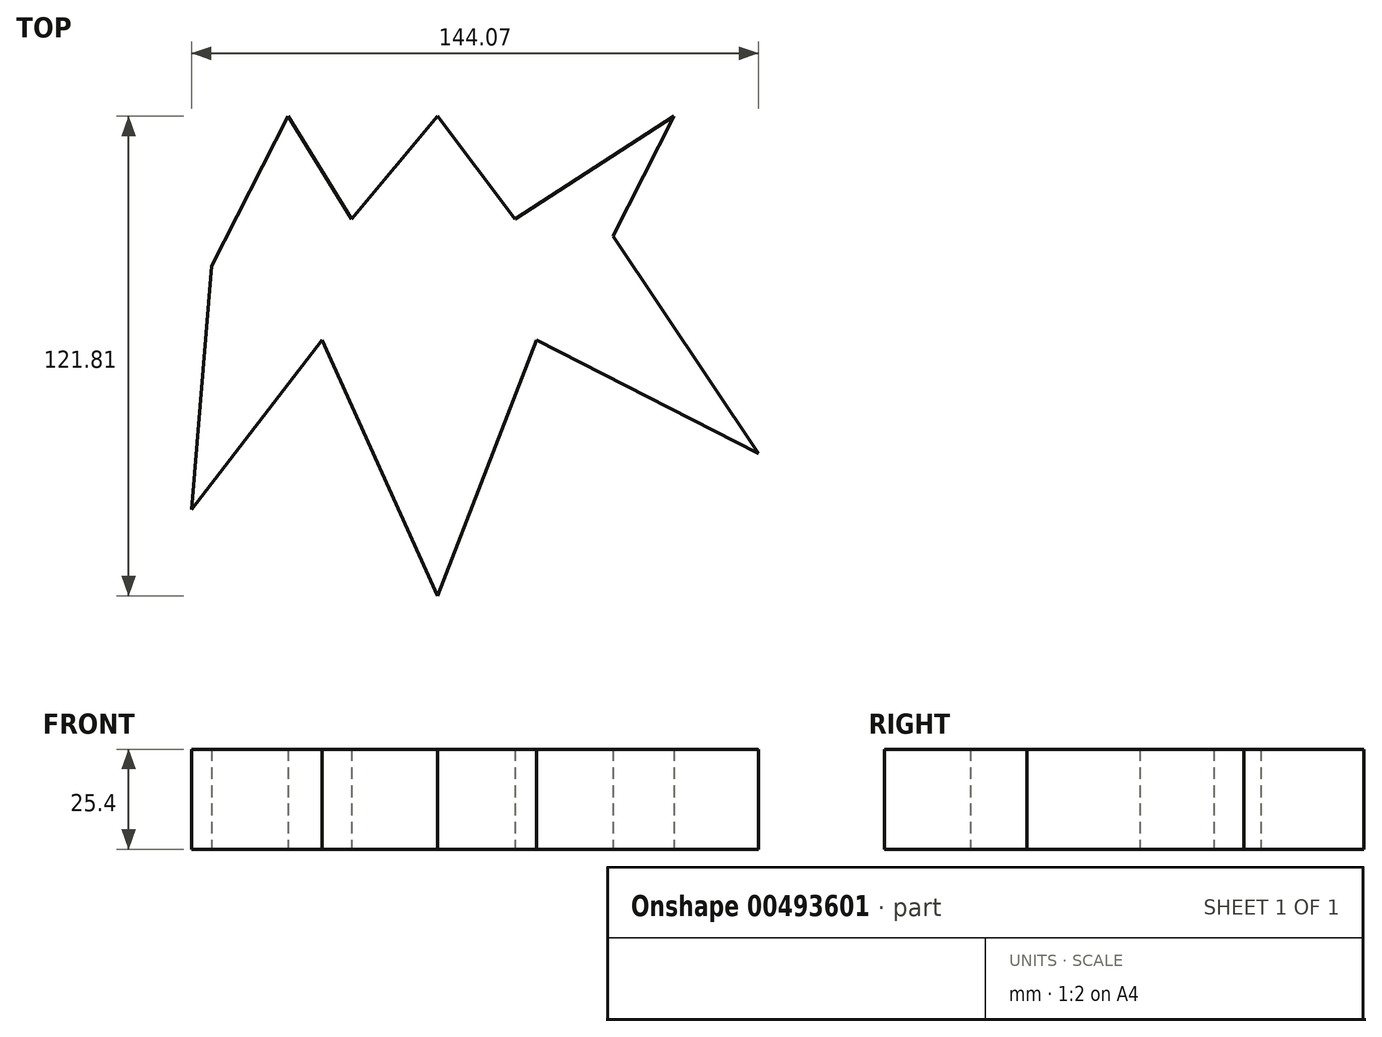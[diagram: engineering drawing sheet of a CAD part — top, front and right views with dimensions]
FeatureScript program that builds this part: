
annotation { "Feature Type Name" : "Feature", "Feature Type Description" : "" }
export const myFeature = defineFeature(function(context is Context, id is Id, definition is map)
    precondition{}
    {
        {
            var Q0;
            Q0=qCreatedBy(makeId("Top.planeOp"),FACE);
            var sketch = newSketch(context, id + "F0", { "sketchPlane" : qUnion([Q0])});
            skLineSegment(sketch, "E0", {"start": v(-67.12, 9.7) * mm, "end": v(-47.69, 47.8) * mm});
            skLineSegment(sketch, "E1", {"start": v(-47.69, 47.8) * mm, "end": v(-31.56, 21.65) * mm});
            skLineSegment(sketch, "E2", {"start": v(-31.56, 21.65) * mm, "end": v(-9.73, 47.8) * mm});
            skLineSegment(sketch, "E3", {"start": v(-9.73, 47.8) * mm, "end": v(9.99, 21.65) * mm});
            skLineSegment(sketch, "E4", {"start": v(9.99, 21.65) * mm, "end": v(50.35, 47.8) * mm});
            skLineSegment(sketch, "E5", {"start": v(50.35, 47.8) * mm, "end": v(34.82, 17.36) * mm});
            skLineSegment(sketch, "E6", {"start": v(34.82, 17.36) * mm, "end": v(71.84, -37.8) * mm});
            skLineSegment(sketch, "E7", {"start": v(71.84, -37.8) * mm, "end": v(15.48, -9.05) * mm});
            skLineSegment(sketch, "E8", {"start": v(15.48, -9.05) * mm, "end": v(-9.77, -74) * mm});
            skLineSegment(sketch, "E9", {"start": v(-9.77, -74) * mm, "end": v(-39.04, -9.05) * mm});
            skLineSegment(sketch, "E10", {"start": v(-39.04, -9.05) * mm, "end": v(-72.23, -52.1) * mm});
            skLineSegment(sketch, "E11", {"start": v(-72.23, -52.1) * mm, "end": v(-67.12, 9.7) * mm});
            skSolve(sketch);
        }
        {
            var Q0;
            Q0=makeQuery(id+"F0.imprint","IMPRINT",FACE,{"disambiguationData":[TD([[makeQuery(id+"F0.imprint","IMPRINT",EDGE,{"derivedFrom":sQuery(id+"F0.wireOp",EDGE,"E0")}),-1.0]])]});
            extrude(context, id + "F1", {"entities" : qUnion([Q0]), "depth" : 25.4 * mm});
        }
    });
